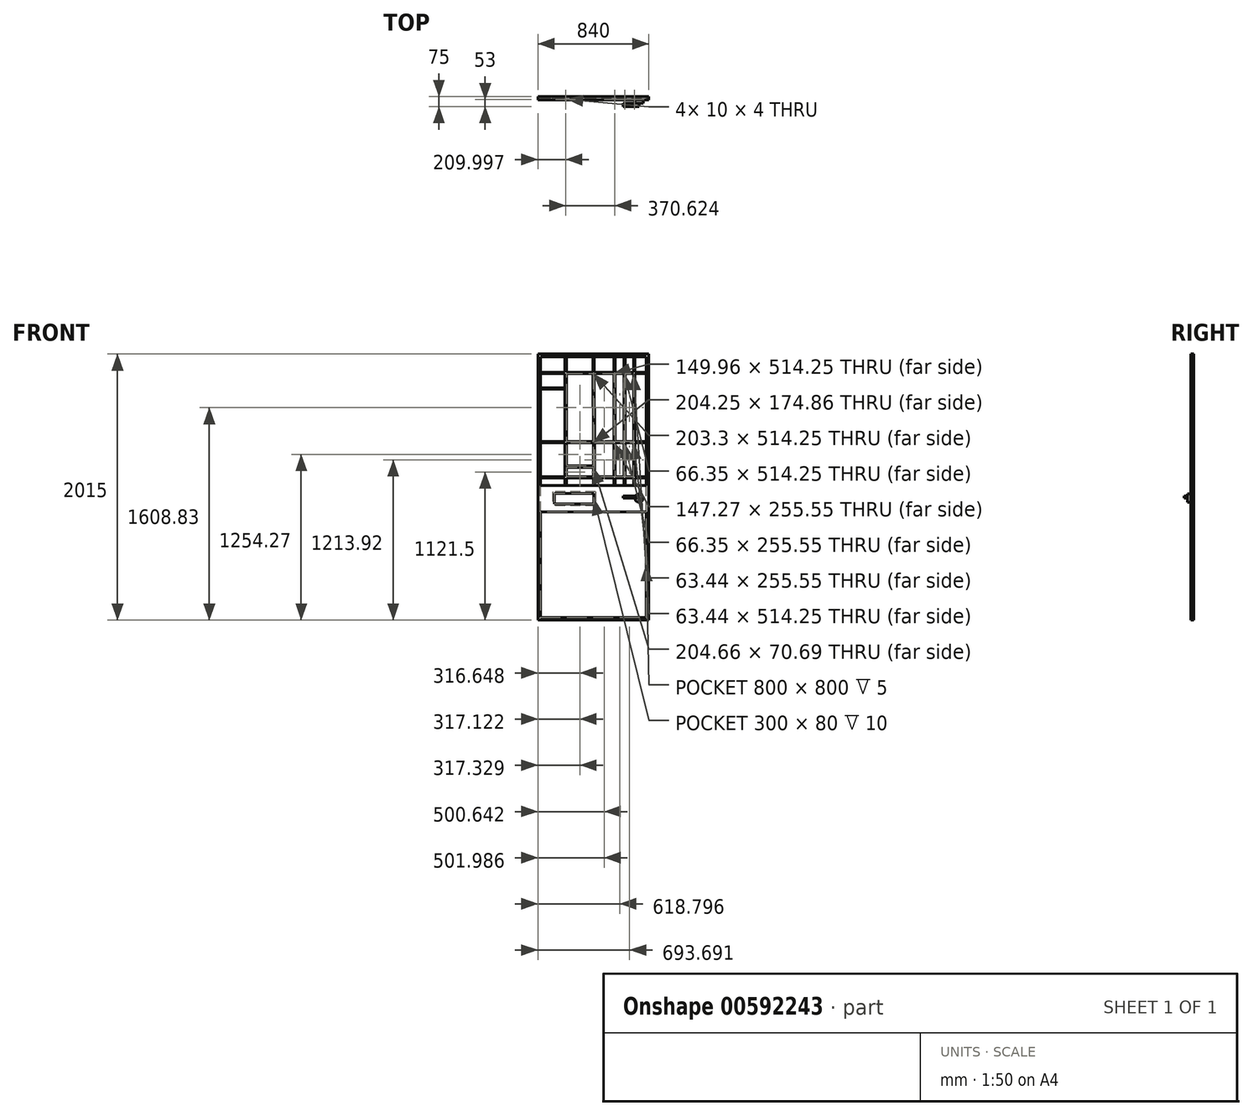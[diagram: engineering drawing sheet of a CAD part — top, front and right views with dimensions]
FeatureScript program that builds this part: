
annotation { "Feature Type Name" : "Feature", "Feature Type Description" : "" }
export const myFeature = defineFeature(function(context is Context, id is Id, definition is map)
    precondition{}
    {
        {
            var Q0;
            Q0=qCreatedBy(makeId("Front.planeOp"),FACE);
            var sketch = newSketch(context, id + "F0", { "sketchPlane" : qUnion([Q0])});
            skLineSegment(sketch, "E0.bottom", {"start": v(0, 0) * mm, "end": v(840, 0) * mm});
            skLineSegment(sketch, "E0.top", {"start": v(0, 2015) * mm, "end": v(840, 2015) * mm});
            skLineSegment(sketch, "E0.left", {"start": v(0, 0) * mm, "end": v(0, 2015) * mm});
            skLineSegment(sketch, "E0.right", {"start": v(840, 0) * mm, "end": v(840, 2015) * mm});
            skLineSegment(sketch, "E1.0", {"start": v(20, 1995) * mm, "end": v(820, 1995) * mm});
            skLineSegment(sketch, "E1.1", {"start": v(20, 20) * mm, "end": v(20, 1995) * mm});
            skLineSegment(sketch, "E1.2", {"start": v(20, 20) * mm, "end": v(820, 20) * mm});
            skLineSegment(sketch, "E1.3", {"start": v(820, 20) * mm, "end": v(820, 1995) * mm});
            skLineSegment(sketch, "E2.bottom", {"start": v(20, 1020) * mm, "end": v(820, 1020) * mm});
            skLineSegment(sketch, "E2.top", {"start": v(20, 820) * mm, "end": v(820, 820) * mm});
            skLineSegment(sketch, "E2.left", {"start": v(20, 1020) * mm, "end": v(20, 820) * mm});
            skLineSegment(sketch, "E2.right", {"start": v(820, 1020) * mm, "end": v(820, 820) * mm});
            skLineSegment(sketch, "E3.bottom", {"start": v(205, 1995) * mm, "end": v(215, 1995) * mm});
            skLineSegment(sketch, "E3.top", {"start": v(205, 1020) * mm, "end": v(215, 1020) * mm});
            skLineSegment(sketch, "E3.left", {"start": v(205, 1995) * mm, "end": v(205, 1875.95) * mm});
            skLineSegment(sketch, "E3.right", {"start": v(215, 1995) * mm, "end": v(215, 1875.95) * mm});
            skLineSegment(sketch, "E4.bottom", {"start": v(735.41, 1995) * mm, "end": v(725.41, 1995) * mm});
            skLineSegment(sketch, "E4.top", {"start": v(735.41, 1020) * mm, "end": v(725.41, 1020) * mm});
            skLineSegment(sketch, "E4.left", {"start": v(735.41, 1995) * mm, "end": v(735.41, 1875.95) * mm});
            skLineSegment(sketch, "E4.right", {"start": v(725.41, 1995) * mm, "end": v(725.41, 1875.95) * mm});
            skLineSegment(sketch, "E5", {"start": v(420, 1995) * mm, "end": v(420, 1930.7) * mm, "construction": true});
            skLineSegment(sketch, "E6.bottom", {"start": v(415, 1995) * mm, "end": v(425, 1995) * mm});
            skLineSegment(sketch, "E6.top", {"start": v(420, 1020) * mm, "end": v(430, 1020) * mm});
            skLineSegment(sketch, "E6.left", {"start": v(415, 1995) * mm, "end": v(415.61, 1875.95) * mm});
            skLineSegment(sketch, "E6.right", {"start": v(425, 1995) * mm, "end": v(428.3, 1351.7) * mm});
            skLineSegment(sketch, "E7.bottom", {"start": v(575.62, 1995) * mm, "end": v(585.62, 1995) * mm});
            skLineSegment(sketch, "E7.top", {"start": v(575.62, 1020) * mm, "end": v(585.62, 1020) * mm});
            skLineSegment(sketch, "E7.left", {"start": v(575.62, 1995) * mm, "end": v(575.62, 1875.95) * mm});
            skLineSegment(sketch, "E7.right", {"start": v(585.62, 1995) * mm, "end": v(585.62, 1875.95) * mm});
            skLineSegment(sketch, "E8.bottom", {"start": v(651.97, 1995) * mm, "end": v(661.97, 1995) * mm});
            skLineSegment(sketch, "E8.top", {"start": v(651.97, 1020) * mm, "end": v(661.97, 1020) * mm});
            skLineSegment(sketch, "E8.left", {"start": v(651.97, 1995) * mm, "end": v(651.97, 1875.95) * mm});
            skLineSegment(sketch, "E8.right", {"start": v(661.97, 1995) * mm, "end": v(661.97, 1875.95) * mm});
            skLineSegment(sketch, "E9.bottom", {"start": v(20, 1875.95) * mm, "end": v(205, 1875.95) * mm});
            skLineSegment(sketch, "E9.top", {"start": v(20, 1865.95) * mm, "end": v(205, 1865.95) * mm});
            skLineSegment(sketch, "E9.left", {"start": v(20, 1875.95) * mm, "end": v(20, 1865.95) * mm});
            skLineSegment(sketch, "E9.right", {"start": v(820, 1875.95) * mm, "end": v(820, 1865.95) * mm});
            skLineSegment(sketch, "E10.bottom", {"start": v(20, 1086.15) * mm, "end": v(205, 1086.15) * mm});
            skLineSegment(sketch, "E10.top", {"start": v(20, 1076.15) * mm, "end": v(205, 1076.15) * mm});
            skLineSegment(sketch, "E10.left", {"start": v(20, 1086.15) * mm, "end": v(20, 1076.15) * mm});
            skLineSegment(sketch, "E10.right", {"start": v(820, 1086.15) * mm, "end": v(820, 1076.15) * mm});
            skLineSegment(sketch, "E11.bottom", {"start": v(215, 1166.84) * mm, "end": v(419.3, 1166.84) * mm});
            skLineSegment(sketch, "E11.top", {"start": v(215, 1156.84) * mm, "end": v(419.3, 1156.84) * mm});
            skLineSegment(sketch, "E12.bottom", {"start": v(20, 1351.7) * mm, "end": v(205, 1351.7) * mm});
            skLineSegment(sketch, "E12.top", {"start": v(20, 1341.7) * mm, "end": v(205, 1341.7) * mm});
            skLineSegment(sketch, "E12.left", {"start": v(20, 1351.7) * mm, "end": v(20, 1341.7) * mm});
            skLineSegment(sketch, "E12.right", {"start": v(820, 1351.7) * mm, "end": v(820, 1341.7) * mm});
            skLineSegment(sketch, "E13.bottom", {"start": v(20, 1757.88) * mm, "end": v(205, 1757.88) * mm});
            skLineSegment(sketch, "E13.top", {"start": v(20, 1747.88) * mm, "end": v(205, 1747.88) * mm});
            skLineSegment(sketch, "E13.left", {"start": v(20, 1757.88) * mm, "end": v(20, 1747.88) * mm});
            skLineSegment(sketch, "E14.trimOffspring", {"start": v(215, 1076.15) * mm, "end": v(419.71, 1076.15) * mm});
            skLineSegment(sketch, "E15.trimOffspring", {"start": v(215, 1086.15) * mm, "end": v(419.66, 1086.15) * mm});
            skLineSegment(sketch, "E16.trimOffspring", {"start": v(215, 1076.15) * mm, "end": v(215, 1020) * mm});
            skLineSegment(sketch, "E17.trimOffspring", {"start": v(205, 1076.15) * mm, "end": v(205, 1020) * mm});
            skLineSegment(sketch, "E18.trimOffspring", {"start": v(419.3, 1156.84) * mm, "end": v(419.66, 1086.15) * mm});
            skLineSegment(sketch, "E19.trimOffspring", {"start": v(419.71, 1076.15) * mm, "end": v(420, 1020) * mm});
            skLineSegment(sketch, "E20.trimOffspring", {"start": v(429.66, 1086.15) * mm, "end": v(575.62, 1086.15) * mm});
            skLineSegment(sketch, "E21.trimOffspring", {"start": v(429.71, 1076.15) * mm, "end": v(430, 1020) * mm});
            skLineSegment(sketch, "E22.trimOffspring", {"start": v(429.71, 1076.15) * mm, "end": v(575.62, 1076.15) * mm});
            skLineSegment(sketch, "E23.trimOffspring", {"start": v(575.62, 1076.15) * mm, "end": v(575.62, 1020) * mm});
            skLineSegment(sketch, "E24.trimOffspring", {"start": v(585.62, 1076.15) * mm, "end": v(585.62, 1020) * mm});
            skLineSegment(sketch, "E25.trimOffspring", {"start": v(585.62, 1086.15) * mm, "end": v(651.97, 1086.15) * mm});
            skLineSegment(sketch, "E26.trimOffspring", {"start": v(585.62, 1076.15) * mm, "end": v(651.97, 1076.15) * mm});
            skLineSegment(sketch, "E27.trimOffspring", {"start": v(651.97, 1076.15) * mm, "end": v(651.97, 1020) * mm});
            skLineSegment(sketch, "E28.trimOffspring", {"start": v(661.97, 1076.15) * mm, "end": v(661.97, 1020) * mm});
            skLineSegment(sketch, "E29.trimOffspring", {"start": v(661.97, 1086.15) * mm, "end": v(725.41, 1086.15) * mm});
            skLineSegment(sketch, "E30.trimOffspring", {"start": v(661.97, 1076.15) * mm, "end": v(725.41, 1076.15) * mm});
            skLineSegment(sketch, "E31.trimOffspring", {"start": v(215, 1156.84) * mm, "end": v(215, 1086.15) * mm});
            skLineSegment(sketch, "E32.trimOffspring", {"start": v(205, 1341.7) * mm, "end": v(205, 1086.15) * mm});
            skLineSegment(sketch, "E33.trimOffspring", {"start": v(215, 1351.7) * mm, "end": v(418.3, 1351.7) * mm});
            skLineSegment(sketch, "E34.trimOffspring", {"start": v(215, 1341.7) * mm, "end": v(418.35, 1341.7) * mm});
            skLineSegment(sketch, "E35.trimOffspring", {"start": v(215, 1341.7) * mm, "end": v(215, 1166.84) * mm});
            skLineSegment(sketch, "E36.trimOffspring", {"start": v(428.35, 1341.7) * mm, "end": v(429.66, 1086.15) * mm});
            skLineSegment(sketch, "E37.trimOffspring", {"start": v(418.35, 1341.7) * mm, "end": v(419.25, 1166.84) * mm});
            skLineSegment(sketch, "E38.trimOffspring", {"start": v(428.35, 1341.7) * mm, "end": v(575.62, 1341.7) * mm});
            skLineSegment(sketch, "E39.trimOffspring", {"start": v(428.3, 1351.7) * mm, "end": v(575.62, 1351.7) * mm});
            skLineSegment(sketch, "E40.trimOffspring", {"start": v(215, 1865.95) * mm, "end": v(215, 1351.7) * mm});
            skLineSegment(sketch, "E41.trimOffspring", {"start": v(215, 1875.95) * mm, "end": v(415.61, 1875.95) * mm});
            skLineSegment(sketch, "E42.trimOffspring", {"start": v(205, 1865.95) * mm, "end": v(205, 1757.88) * mm});
            skLineSegment(sketch, "E43.trimOffspring", {"start": v(215, 1865.95) * mm, "end": v(415.66, 1865.95) * mm});
            skLineSegment(sketch, "E44.trimOffspring", {"start": v(205, 1747.88) * mm, "end": v(205, 1351.7) * mm});
            skLineSegment(sketch, "E45.trimOffspring", {"start": v(425.61, 1875.95) * mm, "end": v(575.62, 1875.95) * mm});
            skLineSegment(sketch, "E46.trimOffspring", {"start": v(415.66, 1865.95) * mm, "end": v(418.3, 1351.7) * mm});
            skLineSegment(sketch, "E47.trimOffspring", {"start": v(425.66, 1865.95) * mm, "end": v(575.62, 1865.95) * mm});
            skLineSegment(sketch, "E48.trimOffspring", {"start": v(575.62, 1865.95) * mm, "end": v(575.62, 1351.7) * mm});
            skLineSegment(sketch, "E49.trimOffspring", {"start": v(585.62, 1875.95) * mm, "end": v(651.97, 1875.95) * mm});
            skLineSegment(sketch, "E50.trimOffspring", {"start": v(585.62, 1865.95) * mm, "end": v(585.62, 1351.7) * mm});
            skLineSegment(sketch, "E51.trimOffspring", {"start": v(585.62, 1865.95) * mm, "end": v(651.97, 1865.95) * mm});
            skLineSegment(sketch, "E52.trimOffspring", {"start": v(651.97, 1865.95) * mm, "end": v(651.97, 1351.7) * mm});
            skLineSegment(sketch, "E53.trimOffspring", {"start": v(661.97, 1875.95) * mm, "end": v(725.41, 1875.95) * mm});
            skLineSegment(sketch, "E54.trimOffspring", {"start": v(661.97, 1865.95) * mm, "end": v(725.41, 1865.95) * mm});
            skLineSegment(sketch, "E55.trimOffspring", {"start": v(661.97, 1865.95) * mm, "end": v(661.97, 1351.7) * mm});
            skLineSegment(sketch, "E56.trimOffspring", {"start": v(725.41, 1865.95) * mm, "end": v(725.41, 1351.7) * mm});
            skLineSegment(sketch, "E57.trimOffspring", {"start": v(735.41, 1875.95) * mm, "end": v(820, 1875.95) * mm});
            skLineSegment(sketch, "E58.trimOffspring", {"start": v(735.41, 1865.95) * mm, "end": v(735.41, 1351.7) * mm});
            skLineSegment(sketch, "E59.trimOffspring", {"start": v(735.41, 1865.95) * mm, "end": v(820, 1865.95) * mm});
            skLineSegment(sketch, "E60.trimOffspring", {"start": v(585.62, 1351.7) * mm, "end": v(651.97, 1351.7) * mm});
            skLineSegment(sketch, "E61.trimOffspring", {"start": v(585.62, 1341.7) * mm, "end": v(651.97, 1341.7) * mm});
            skLineSegment(sketch, "E62.trimOffspring", {"start": v(575.62, 1341.7) * mm, "end": v(575.62, 1086.15) * mm});
            skLineSegment(sketch, "E63.trimOffspring", {"start": v(585.62, 1341.7) * mm, "end": v(585.62, 1086.15) * mm});
            skLineSegment(sketch, "E64.trimOffspring", {"start": v(651.97, 1341.7) * mm, "end": v(651.97, 1086.15) * mm});
            skLineSegment(sketch, "E65.trimOffspring", {"start": v(661.97, 1351.7) * mm, "end": v(725.41, 1351.7) * mm});
            skLineSegment(sketch, "E66.trimOffspring", {"start": v(661.97, 1341.7) * mm, "end": v(725.41, 1341.7) * mm});
            skLineSegment(sketch, "E67.trimOffspring", {"start": v(661.97, 1341.7) * mm, "end": v(661.97, 1086.15) * mm});
            skLineSegment(sketch, "E68.trimOffspring", {"start": v(725.41, 1341.7) * mm, "end": v(725.41, 1086.15) * mm});
            skLineSegment(sketch, "E69.trimOffspring", {"start": v(735.41, 1351.7) * mm, "end": v(820, 1351.7) * mm});
            skLineSegment(sketch, "E70.trimOffspring", {"start": v(735.41, 1341.7) * mm, "end": v(735.41, 1086.15) * mm});
            skLineSegment(sketch, "E71.trimOffspring", {"start": v(735.41, 1341.7) * mm, "end": v(820, 1341.7) * mm});
            skLineSegment(sketch, "E72.trimOffspring", {"start": v(735.41, 1076.15) * mm, "end": v(820, 1076.15) * mm});
            skLineSegment(sketch, "E73.trimOffspring", {"start": v(735.41, 1086.15) * mm, "end": v(820, 1086.15) * mm});
            skLineSegment(sketch, "E74.trimOffspring", {"start": v(735.41, 1076.15) * mm, "end": v(735.41, 1020) * mm});
            skLineSegment(sketch, "E75.trimOffspring", {"start": v(725.41, 1076.15) * mm, "end": v(725.41, 1020) * mm});
            skSolve(sketch);
        }
        {
            var Q0;
            Q0 = qSketchRegion(id + "F0", true);
            extrude(context, id + "F1", {"entities" : qUnion([Q0]), "oppositeDirection" : true, "depth" : 20 * mm, "offsetDistance" : 25 * mm, "hasSecondDirection" : true, "secondDirectionOppositeDirection" : false, "secondDirectionDepth" : 5 * mm});
        }
        {
            var Q0;
            {var subQ0=sQuery(id+"F0.wireOp",EDGE,"E1.2");Q0=makeQuery(id+"F0.imprint","IMPRINT",FACE,{"disambiguationData":[TD([[makeQuery(id+"F0.imprint","IMPRINT",EDGE,{"derivedFrom":subQ0}),1.0]])]});}
            extrude(context, id + "F2", {"entities" : qUnion([Q0]), "operationType" : NewBodyOperationType.ADD, "oppositeDirection" : true, "depth" : 5 * mm, "offsetDistance" : 25 * mm});
        }
        {
            var Q0;
            Q0=makeQuery(id+"F0.imprint","IMPRINT",FACE,{"disambiguationData":[TD([[makeQuery(id+"F0.imprint","IMPRINT",EDGE,{"derivedFrom":sQuery(id+"F0.wireOp",EDGE,"E2.top")}),1.0]])]});
            extrude(context, id + "F3", {"entities" : qUnion([Q0]), "operationType" : NewBodyOperationType.ADD, "depth" : 5 * mm, "offsetDistance" : 25 * mm, "hasSecondDirection" : true, "secondDirectionOppositeDirection" : true, "secondDirectionDepth" : 5 * mm});
        }
        {
            var Q0;
            Q0=makeQuery(id+"F0.imprint","IMPRINT",FACE,{"disambiguationData":[TD([[makeQuery(id+"F0.imprint","IMPRINT",EDGE,{"derivedFrom":sQuery(id+"F0.wireOp",EDGE,"E3.bottom")}),-1.0]])]});
            var Q1;
            Q1=makeQuery(id+"F0.imprint","IMPRINT",FACE,{"disambiguationData":[TD([[makeQuery(id+"F0.imprint","IMPRINT",EDGE,{"derivedFrom":sQuery(id+"F0.wireOp",EDGE,"E6.bottom")}),-1.0]])]});
            var Q2;
            Q2=makeQuery(id+"F0.imprint","IMPRINT",FACE,{"disambiguationData":[TD([[makeQuery(id+"F0.imprint","IMPRINT",EDGE,{"derivedFrom":sQuery(id+"F0.wireOp",EDGE,"E4.bottom")}),1.0]])]});
            var Q3;
            {var subQ5=sQuery(id+"F0.wireOp",EDGE,"E9.left");Q3=makeQuery(id+"F0.imprint","IMPRINT",FACE,{"disambiguationData":[TD([[makeQuery(id+"F0.imprint","IMPRINT",EDGE,{"derivedFrom":subQ5}),1.0]])]});}
            var Q4;
            {var subQ0=sQuery(id+"F0.wireOp",EDGE,"E9.bottom");var subQ1=sQuery(id+"F0.wireOp",EDGE,"E3.left");var subQ2=makeQuery(id+"F0.imprint","INTERSECT",VERTEX,{"derivedFrom":[subQ1,subQ0]});Q4=makeQuery(id+"F0.imprint","IMPRINT",FACE,{"disambiguationData":[TD([[makeQuery(id+"F0.imprint","IMPRINT",EDGE,{"disambiguationData":[TD([[subQ2,-1.0]])],"derivedFrom":subQ1}),1.0]])]});}
            var Q5;
            {var subQ0=sQuery(id+"F0.wireOp",EDGE,"E9.bottom");var subQ1=sQuery(id+"F0.wireOp",EDGE,"E6.left");var subQ2=makeQuery(id+"F0.imprint","INTERSECT",VERTEX,{"derivedFrom":[subQ1,subQ0]});Q5=makeQuery(id+"F0.imprint","IMPRINT",FACE,{"disambiguationData":[TD([[makeQuery(id+"F0.imprint","IMPRINT",EDGE,{"disambiguationData":[TD([[subQ2,-1.0]])],"derivedFrom":subQ1}),1.0]])]});}
            var Q6;
            {var subQ0=sQuery(id+"F0.wireOp",EDGE,"E9.top");var subQ1=sQuery(id+"F0.wireOp",EDGE,"E6.left");var subQ2=makeQuery(id+"F0.imprint","INTERSECT",VERTEX,{"derivedFrom":[subQ1,subQ0]});Q6=makeQuery(id+"F0.imprint","IMPRINT",FACE,{"disambiguationData":[TD([[makeQuery(id+"F0.imprint","IMPRINT",EDGE,{"disambiguationData":[TD([[subQ2,-1.0]])],"derivedFrom":subQ1}),1.0]])]});}
            var Q7;
            {var subQ7=sQuery(id+"F0.wireOp",EDGE,"E13.right");Q7=makeQuery(id+"F0.imprint","IMPRINT",FACE,{"disambiguationData":[TD([[makeQuery(id+"F0.imprint","IMPRINT",EDGE,{"derivedFrom":subQ7}),1.0]])]});}
            var Q8;
            Q8=makeQuery(id+"F0.imprint","IMPRINT",FACE,{"disambiguationData":[TD([[makeQuery(id+"F0.imprint","IMPRINT",EDGE,{"derivedFrom":sQuery(id+"F0.wireOp",EDGE,"E13.bottom")}),-1.0]])]});
            var Q9;
            {var subQ0=sQuery(id+"F0.wireOp",EDGE,"E7.bottom");Q9=makeQuery(id+"F0.imprint","IMPRINT",FACE,{"disambiguationData":[TD([[makeQuery(id+"F0.imprint","IMPRINT",EDGE,{"derivedFrom":subQ0}),-1.0]])]});}
            var Q10;
            {var subQ0=sQuery(id+"F0.wireOp",EDGE,"E8.bottom");Q10=makeQuery(id+"F0.imprint","IMPRINT",FACE,{"disambiguationData":[TD([[makeQuery(id+"F0.imprint","IMPRINT",EDGE,{"derivedFrom":subQ0}),-1.0]])]});}
            var Q11;
            {var subQ0=sQuery(id+"F0.wireOp",EDGE,"E9.top");var subQ1=sQuery(id+"F0.wireOp",EDGE,"E8.left");var subQ2=makeQuery(id+"F0.imprint","INTERSECT",VERTEX,{"derivedFrom":[subQ1,subQ0]});Q11=makeQuery(id+"F0.imprint","IMPRINT",FACE,{"disambiguationData":[TD([[makeQuery(id+"F0.imprint","IMPRINT",EDGE,{"disambiguationData":[TD([[subQ2,-1.0]])],"derivedFrom":subQ1}),1.0]])]});}
            var Q12;
            {var subQ0=sQuery(id+"F0.wireOp",EDGE,"E9.bottom");var subQ1=sQuery(id+"F0.wireOp",EDGE,"E8.left");var subQ2=makeQuery(id+"F0.imprint","INTERSECT",VERTEX,{"derivedFrom":[subQ1,subQ0]});Q12=makeQuery(id+"F0.imprint","IMPRINT",FACE,{"disambiguationData":[TD([[makeQuery(id+"F0.imprint","IMPRINT",EDGE,{"disambiguationData":[TD([[subQ2,-1.0]])],"derivedFrom":subQ1}),1.0]])]});}
            var Q13;
            {var subQ0=sQuery(id+"F0.wireOp",EDGE,"E9.top");var subQ1=sQuery(id+"F0.wireOp",EDGE,"E7.left");var subQ2=makeQuery(id+"F0.imprint","INTERSECT",VERTEX,{"derivedFrom":[subQ1,subQ0]});Q13=makeQuery(id+"F0.imprint","IMPRINT",FACE,{"disambiguationData":[TD([[makeQuery(id+"F0.imprint","IMPRINT",EDGE,{"disambiguationData":[TD([[subQ2,-1.0]])],"derivedFrom":subQ1}),1.0]])]});}
            var Q14;
            {var subQ5=sQuery(id+"F0.wireOp",EDGE,"E9.right");Q14=makeQuery(id+"F0.imprint","IMPRINT",FACE,{"disambiguationData":[TD([[makeQuery(id+"F0.imprint","IMPRINT",EDGE,{"derivedFrom":subQ5}),-1.0]])]});}
            var Q15;
            {var subQ0=sQuery(id+"F0.wireOp",EDGE,"E9.top");var subQ1=sQuery(id+"F0.wireOp",EDGE,"E4.left");var subQ2=makeQuery(id+"F0.imprint","INTERSECT",VERTEX,{"derivedFrom":[subQ1,subQ0]});Q15=makeQuery(id+"F0.imprint","IMPRINT",FACE,{"disambiguationData":[TD([[makeQuery(id+"F0.imprint","IMPRINT",EDGE,{"disambiguationData":[TD([[subQ2,-1.0]])],"derivedFrom":subQ1}),-1.0]])]});}
            var Q16;
            {var subQ0=sQuery(id+"F0.wireOp",EDGE,"E9.bottom");var subQ1=sQuery(id+"F0.wireOp",EDGE,"E4.left");var subQ2=makeQuery(id+"F0.imprint","INTERSECT",VERTEX,{"derivedFrom":[subQ1,subQ0]});Q16=makeQuery(id+"F0.imprint","IMPRINT",FACE,{"disambiguationData":[TD([[makeQuery(id+"F0.imprint","IMPRINT",EDGE,{"disambiguationData":[TD([[subQ2,-1.0]])],"derivedFrom":subQ1}),-1.0]])]});}
            var Q17;
            {var subQ0=sQuery(id+"F0.wireOp",EDGE,"E9.bottom");var subQ1=sQuery(id+"F0.wireOp",EDGE,"E7.left");var subQ2=makeQuery(id+"F0.imprint","INTERSECT",VERTEX,{"derivedFrom":[subQ1,subQ0]});Q17=makeQuery(id+"F0.imprint","IMPRINT",FACE,{"disambiguationData":[TD([[makeQuery(id+"F0.imprint","IMPRINT",EDGE,{"disambiguationData":[TD([[subQ2,-1.0]])],"derivedFrom":subQ1}),1.0]])]});}
            var Q18;
            {var subQ5=sQuery(id+"F0.wireOp",EDGE,"E12.left");Q18=makeQuery(id+"F0.imprint","IMPRINT",FACE,{"disambiguationData":[TD([[makeQuery(id+"F0.imprint","IMPRINT",EDGE,{"derivedFrom":subQ5}),1.0]])]});}
            var Q19;
            {var subQ0=sQuery(id+"F0.wireOp",EDGE,"E11.left");Q19=makeQuery(id+"F0.imprint","IMPRINT",FACE,{"disambiguationData":[TD([[makeQuery(id+"F0.imprint","IMPRINT",EDGE,{"derivedFrom":subQ0}),-1.0]])]});}
            var Q20;
            {var subQ0=sQuery(id+"F0.wireOp",EDGE,"E12.bottom");var subQ1=sQuery(id+"F0.wireOp",EDGE,"E3.left");var subQ2=makeQuery(id+"F0.imprint","INTERSECT",VERTEX,{"derivedFrom":[subQ1,subQ0]});Q20=makeQuery(id+"F0.imprint","IMPRINT",FACE,{"disambiguationData":[TD([[makeQuery(id+"F0.imprint","IMPRINT",EDGE,{"disambiguationData":[TD([[subQ2,-1.0]])],"derivedFrom":subQ1}),1.0]])]});}
            var Q21;
            {var subQ5=sQuery(id+"F0.wireOp",EDGE,"E11.right");Q21=makeQuery(id+"F0.imprint","IMPRINT",FACE,{"disambiguationData":[TD([[makeQuery(id+"F0.imprint","IMPRINT",EDGE,{"derivedFrom":subQ5}),1.0]])]});}
            var Q22;
            {var subQ0=sQuery(id+"F0.wireOp",EDGE,"E12.bottom");var subQ1=sQuery(id+"F0.wireOp",EDGE,"E6.left");var subQ2=makeQuery(id+"F0.imprint","INTERSECT",VERTEX,{"derivedFrom":[subQ1,subQ0]});Q22=makeQuery(id+"F0.imprint","IMPRINT",FACE,{"disambiguationData":[TD([[makeQuery(id+"F0.imprint","IMPRINT",EDGE,{"disambiguationData":[TD([[subQ2,-1.0]])],"derivedFrom":subQ1}),1.0]])]});}
            var Q23;
            {var subQ0=sQuery(id+"F0.wireOp",EDGE,"E12.bottom");var subQ1=sQuery(id+"F0.wireOp",EDGE,"E7.left");var subQ2=makeQuery(id+"F0.imprint","INTERSECT",VERTEX,{"derivedFrom":[subQ1,subQ0]});Q23=makeQuery(id+"F0.imprint","IMPRINT",FACE,{"disambiguationData":[TD([[makeQuery(id+"F0.imprint","IMPRINT",EDGE,{"disambiguationData":[TD([[subQ2,-1.0]])],"derivedFrom":subQ1}),1.0]])]});}
            var Q24;
            {var subQ0=sQuery(id+"F0.wireOp",EDGE,"E12.bottom");var subQ1=sQuery(id+"F0.wireOp",EDGE,"E8.left");var subQ2=makeQuery(id+"F0.imprint","INTERSECT",VERTEX,{"derivedFrom":[subQ1,subQ0]});Q24=makeQuery(id+"F0.imprint","IMPRINT",FACE,{"disambiguationData":[TD([[makeQuery(id+"F0.imprint","IMPRINT",EDGE,{"disambiguationData":[TD([[subQ2,-1.0]])],"derivedFrom":subQ1}),1.0]])]});}
            var Q25;
            {var subQ0=sQuery(id+"F0.wireOp",EDGE,"E12.bottom");var subQ1=sQuery(id+"F0.wireOp",EDGE,"E4.left");var subQ2=makeQuery(id+"F0.imprint","INTERSECT",VERTEX,{"derivedFrom":[subQ1,subQ0]});Q25=makeQuery(id+"F0.imprint","IMPRINT",FACE,{"disambiguationData":[TD([[makeQuery(id+"F0.imprint","IMPRINT",EDGE,{"disambiguationData":[TD([[subQ2,-1.0]])],"derivedFrom":subQ1}),-1.0]])]});}
            var Q26;
            {var subQ5=sQuery(id+"F0.wireOp",EDGE,"E12.right");Q26=makeQuery(id+"F0.imprint","IMPRINT",FACE,{"disambiguationData":[TD([[makeQuery(id+"F0.imprint","IMPRINT",EDGE,{"derivedFrom":subQ5}),-1.0]])]});}
            var Q27;
            {var subQ0=sQuery(id+"F0.wireOp",EDGE,"E12.top");var subQ1=sQuery(id+"F0.wireOp",EDGE,"E4.left");var subQ2=makeQuery(id+"F0.imprint","INTERSECT",VERTEX,{"derivedFrom":[subQ1,subQ0]});Q27=makeQuery(id+"F0.imprint","IMPRINT",FACE,{"disambiguationData":[TD([[makeQuery(id+"F0.imprint","IMPRINT",EDGE,{"disambiguationData":[TD([[subQ2,-1.0]])],"derivedFrom":subQ1}),-1.0]])]});}
            var Q28;
            {var subQ0=sQuery(id+"F0.wireOp",EDGE,"E12.top");var subQ1=sQuery(id+"F0.wireOp",EDGE,"E8.left");var subQ2=makeQuery(id+"F0.imprint","INTERSECT",VERTEX,{"derivedFrom":[subQ1,subQ0]});Q28=makeQuery(id+"F0.imprint","IMPRINT",FACE,{"disambiguationData":[TD([[makeQuery(id+"F0.imprint","IMPRINT",EDGE,{"disambiguationData":[TD([[subQ2,-1.0]])],"derivedFrom":subQ1}),1.0]])]});}
            var Q29;
            {var subQ0=sQuery(id+"F0.wireOp",EDGE,"E12.top");var subQ1=sQuery(id+"F0.wireOp",EDGE,"E7.left");var subQ2=makeQuery(id+"F0.imprint","INTERSECT",VERTEX,{"derivedFrom":[subQ1,subQ0]});Q29=makeQuery(id+"F0.imprint","IMPRINT",FACE,{"disambiguationData":[TD([[makeQuery(id+"F0.imprint","IMPRINT",EDGE,{"disambiguationData":[TD([[subQ2,-1.0]])],"derivedFrom":subQ1}),1.0]])]});}
            var Q30;
            {var subQ0=sQuery(id+"F0.wireOp",EDGE,"E4.top");Q30=makeQuery(id+"F0.imprint","IMPRINT",FACE,{"disambiguationData":[TD([[makeQuery(id+"F0.imprint","IMPRINT",EDGE,{"derivedFrom":subQ0}),-1.0]])]});}
            var Q31;
            {var subQ5=sQuery(id+"F0.wireOp",EDGE,"E10.right");Q31=makeQuery(id+"F0.imprint","IMPRINT",FACE,{"disambiguationData":[TD([[makeQuery(id+"F0.imprint","IMPRINT",EDGE,{"derivedFrom":subQ5}),-1.0]])]});}
            var Q32;
            {var subQ0=sQuery(id+"F0.wireOp",EDGE,"E10.bottom");var subQ1=sQuery(id+"F0.wireOp",EDGE,"E4.left");var subQ2=makeQuery(id+"F0.imprint","INTERSECT",VERTEX,{"derivedFrom":[subQ1,subQ0]});Q32=makeQuery(id+"F0.imprint","IMPRINT",FACE,{"disambiguationData":[TD([[makeQuery(id+"F0.imprint","IMPRINT",EDGE,{"disambiguationData":[TD([[subQ2,-1.0]])],"derivedFrom":subQ1}),-1.0]])]});}
            var Q33;
            {var subQ0=sQuery(id+"F0.wireOp",EDGE,"E10.bottom");var subQ1=sQuery(id+"F0.wireOp",EDGE,"E8.left");var subQ2=makeQuery(id+"F0.imprint","INTERSECT",VERTEX,{"derivedFrom":[subQ1,subQ0]});Q33=makeQuery(id+"F0.imprint","IMPRINT",FACE,{"disambiguationData":[TD([[makeQuery(id+"F0.imprint","IMPRINT",EDGE,{"disambiguationData":[TD([[subQ2,-1.0]])],"derivedFrom":subQ1}),1.0]])]});}
            var Q34;
            {var subQ0=sQuery(id+"F0.wireOp",EDGE,"E8.top");Q34=makeQuery(id+"F0.imprint","IMPRINT",FACE,{"disambiguationData":[TD([[makeQuery(id+"F0.imprint","IMPRINT",EDGE,{"derivedFrom":subQ0}),1.0]])]});}
            var Q35;
            {var subQ0=sQuery(id+"F0.wireOp",EDGE,"E10.bottom");var subQ1=sQuery(id+"F0.wireOp",EDGE,"E7.left");var subQ2=makeQuery(id+"F0.imprint","INTERSECT",VERTEX,{"derivedFrom":[subQ1,subQ0]});Q35=makeQuery(id+"F0.imprint","IMPRINT",FACE,{"disambiguationData":[TD([[makeQuery(id+"F0.imprint","IMPRINT",EDGE,{"disambiguationData":[TD([[subQ2,-1.0]])],"derivedFrom":subQ1}),1.0]])]});}
            var Q36;
            {var subQ0=sQuery(id+"F0.wireOp",EDGE,"E7.top");Q36=makeQuery(id+"F0.imprint","IMPRINT",FACE,{"disambiguationData":[TD([[makeQuery(id+"F0.imprint","IMPRINT",EDGE,{"derivedFrom":subQ0}),1.0]])]});}
            var Q37;
            {var subQ0=sQuery(id+"F0.wireOp",EDGE,"E6.top");Q37=makeQuery(id+"F0.imprint","IMPRINT",FACE,{"disambiguationData":[TD([[makeQuery(id+"F0.imprint","IMPRINT",EDGE,{"derivedFrom":subQ0}),1.0]])]});}
            var Q38;
            {var subQ5=sQuery(id+"F0.wireOp",EDGE,"E10.left");Q38=makeQuery(id+"F0.imprint","IMPRINT",FACE,{"disambiguationData":[TD([[makeQuery(id+"F0.imprint","IMPRINT",EDGE,{"derivedFrom":subQ5}),1.0]])]});}
            var Q39;
            {var subQ0=sQuery(id+"F0.wireOp",EDGE,"E3.top");Q39=makeQuery(id+"F0.imprint","IMPRINT",FACE,{"disambiguationData":[TD([[makeQuery(id+"F0.imprint","IMPRINT",EDGE,{"derivedFrom":subQ0}),1.0]])]});}
            var Q40;
            {var subQ0=sQuery(id+"F0.wireOp",EDGE,"E10.bottom");var subQ1=sQuery(id+"F0.wireOp",EDGE,"E6.left");var subQ2=makeQuery(id+"F0.imprint","INTERSECT",VERTEX,{"derivedFrom":[subQ1,subQ0]});Q40=makeQuery(id+"F0.imprint","IMPRINT",FACE,{"disambiguationData":[TD([[makeQuery(id+"F0.imprint","IMPRINT",EDGE,{"disambiguationData":[TD([[subQ2,-1.0]])],"derivedFrom":subQ1}),1.0]])]});}
            var Q41;
            {var subQ0=sQuery(id+"F0.wireOp",EDGE,"E10.bottom");var subQ1=sQuery(id+"F0.wireOp",EDGE,"E3.left");var subQ2=makeQuery(id+"F0.imprint","INTERSECT",VERTEX,{"derivedFrom":[subQ1,subQ0]});Q41=makeQuery(id+"F0.imprint","IMPRINT",FACE,{"disambiguationData":[TD([[makeQuery(id+"F0.imprint","IMPRINT",EDGE,{"disambiguationData":[TD([[subQ2,-1.0]])],"derivedFrom":subQ1}),1.0]])]});}
            var Q42;
            {var subQ0=sQuery(id+"F0.wireOp",EDGE,"E11.top");Q42=makeQuery(id+"F0.imprint","IMPRINT",FACE,{"disambiguationData":[TD([[makeQuery(id+"F0.imprint","IMPRINT",EDGE,{"derivedFrom":subQ0}),1.0]])]});}
            extrude(context, id + "F4", {"entities" : qUnion([Q0, Q1, Q2, Q3, Q4, Q5, Q6, Q7, Q8, Q9, Q10, Q11, Q12, Q13, Q14, Q15, Q16, Q17, Q18, Q19, Q20, Q21, Q22, Q23, Q24, Q25, Q26, Q27, Q28, Q29, Q30, Q31, Q32, Q33, Q34, Q35, Q36, Q37, Q38, Q39, Q40, Q41, Q42]), "operationType" : NewBodyOperationType.ADD, "depth" : 4 * mm, "offsetDistance" : 25 * mm});
        }
        {
            var Q0;
            {var subQ0=sQuery(id+"F0.wireOp",EDGE,"E2.right");var subQ1=sQuery(id+"F0.wireOp",EDGE,"E2.left");Q0=makeQuery(id+"F3.boolean.opBoolean","MERGE",FACE,{"derivedFrom":[makeQuery(id+"F1.opExtrude","CAP_FACE",FACE,{"disambiguationData":[OSD([sQuery(id+"F0.wireOp",EDGE,"E0.bottom"),sQuery(id+"F0.wireOp",EDGE,"E0.top"),sQuery(id+"F0.wireOp",EDGE,"E0.left"),sQuery(id+"F0.wireOp",EDGE,"E0.right"),sQuery(id+"F0.wireOp",EDGE,"E1.0"),sQuery(id+"F0.wireOp",EDGE,"E1.1"),sQuery(id+"F0.wireOp",EDGE,"E1.2"),sQuery(id+"F0.wireOp",EDGE,"E1.3"),subQ1,subQ0,sQuery(id+"F0.wireOp",EDGE,"E3.bottom"),sQuery(id+"F0.wireOp",EDGE,"E4.bottom"),sQuery(id+"F0.wireOp",EDGE,"E6.bottom"),sQuery(id+"F0.wireOp",EDGE,"E7.bottom"),sQuery(id+"F0.wireOp",EDGE,"E8.bottom"),sQuery(id+"F0.wireOp",EDGE,"E9.left"),sQuery(id+"F0.wireOp",EDGE,"E9.right"),sQuery(id+"F0.wireOp",EDGE,"E10.left"),sQuery(id+"F0.wireOp",EDGE,"E10.right"),sQuery(id+"F0.wireOp",EDGE,"E12.left"),sQuery(id+"F0.wireOp",EDGE,"E12.right"),sQuery(id+"F0.wireOp",EDGE,"E13.left")])],"isStart":true}),makeQuery(id+"F3.opExtrude","CAP_FACE",FACE,{"disambiguationData":[OSD([sQuery(id+"F0.wireOp",EDGE,"E2.bottom"),sQuery(id+"F0.wireOp",EDGE,"E2.top"),subQ1,subQ0,sQuery(id+"F0.wireOp",EDGE,"E3.top"),sQuery(id+"F0.wireOp",EDGE,"E4.top"),sQuery(id+"F0.wireOp",EDGE,"E6.top"),sQuery(id+"F0.wireOp",EDGE,"E7.top"),sQuery(id+"F0.wireOp",EDGE,"E8.top")])],"isStart":false})]});}
            var sketch = newSketch(context, id + "F5", { "sketchPlane" : qUnion([Q0])});
            skLineSegment(sketch, "E76.bottom", {"start": v(123.41, 960) * mm, "end": v(423.41, 960) * mm});
            skLineSegment(sketch, "E76.top", {"start": v(123.41, 880) * mm, "end": v(423.41, 880) * mm});
            skLineSegment(sketch, "E76.left", {"start": v(123.41, 960) * mm, "end": v(123.41, 880) * mm});
            skLineSegment(sketch, "E76.right", {"start": v(423.41, 960) * mm, "end": v(423.41, 880) * mm});
            skSolve(sketch);
        }
        {
            var Q0;
            Q0=makeQuery(id+"F5.imprint","IMPRINT",FACE,{"disambiguationData":[TD([[makeQuery(id+"F5.imprint","IMPRINT",EDGE,{"derivedFrom":sQuery(id+"F5.wireOp",EDGE,"E76.bottom")}),-1.0]])]});
            extrude(context, id + "F6", {"entities" : qUnion([Q0]), "operationType" : NewBodyOperationType.REMOVE, "oppositeDirection" : true, "depth" : 25 * mm, "offsetDistance" : 25 * mm});
        }
        {
            var Q0;
            {var subQ0=sQuery(id+"F0.wireOp",EDGE,"E2.right");var subQ1=sQuery(id+"F0.wireOp",EDGE,"E2.left");Q0=makeQuery(id+"F3.boolean.opBoolean","MERGE",FACE,{"derivedFrom":[makeQuery(id+"F1.opExtrude","CAP_FACE",FACE,{"disambiguationData":[OSD([sQuery(id+"F0.wireOp",EDGE,"E0.bottom"),sQuery(id+"F0.wireOp",EDGE,"E0.top"),sQuery(id+"F0.wireOp",EDGE,"E0.left"),sQuery(id+"F0.wireOp",EDGE,"E0.right"),sQuery(id+"F0.wireOp",EDGE,"E1.0"),sQuery(id+"F0.wireOp",EDGE,"E1.1"),sQuery(id+"F0.wireOp",EDGE,"E1.2"),sQuery(id+"F0.wireOp",EDGE,"E1.3"),subQ1,subQ0,sQuery(id+"F0.wireOp",EDGE,"E3.bottom"),sQuery(id+"F0.wireOp",EDGE,"E4.bottom"),sQuery(id+"F0.wireOp",EDGE,"E6.bottom"),sQuery(id+"F0.wireOp",EDGE,"E7.bottom"),sQuery(id+"F0.wireOp",EDGE,"E8.bottom"),sQuery(id+"F0.wireOp",EDGE,"E9.left"),sQuery(id+"F0.wireOp",EDGE,"E9.right"),sQuery(id+"F0.wireOp",EDGE,"E10.left"),sQuery(id+"F0.wireOp",EDGE,"E10.right"),sQuery(id+"F0.wireOp",EDGE,"E12.left"),sQuery(id+"F0.wireOp",EDGE,"E12.right"),sQuery(id+"F0.wireOp",EDGE,"E13.left")])],"isStart":true}),makeQuery(id+"F3.opExtrude","CAP_FACE",FACE,{"disambiguationData":[OSD([sQuery(id+"F0.wireOp",EDGE,"E2.bottom"),sQuery(id+"F0.wireOp",EDGE,"E2.top"),subQ1,subQ0,sQuery(id+"F0.wireOp",EDGE,"E3.top"),sQuery(id+"F0.wireOp",EDGE,"E4.top"),sQuery(id+"F0.wireOp",EDGE,"E6.top"),sQuery(id+"F0.wireOp",EDGE,"E7.top"),sQuery(id+"F0.wireOp",EDGE,"E8.top")])],"isStart":false})]});}
            var sketch = newSketch(context, id + "F7", { "sketchPlane" : qUnion([Q0])});
            skCircle(sketch, "E77", {"center": v(765.68, 923.55) * mm, "radius": 31.49 * mm});
            skSolve(sketch);
        }
        {
            var Q0;
            Q0 = qSketchRegion(id + "F7", true);
            extrude(context, id + "F8", {"entities" : qUnion([Q0]), "operationType" : NewBodyOperationType.ADD, "depth" : 25 * mm, "offsetDistance" : 25 * mm});
        }
        {
            var Q0;
            Q0=makeQuery(id+"F8.opExtrude","CAP_FACE",FACE,{"disambiguationData":[OSD([sQuery(id+"F7.wireOp",EDGE,"E77")])],"isStart":false});
            var sketch = newSketch(context, id + "F9", { "sketchPlane" : qUnion([Q0])});
            skLineSegment(sketch, "E78.bottom", {"start": v(765.68, 923.55) * mm, "end": v(644.2, 923.55) * mm});
            skLineSegment(sketch, "E78.top", {"start": v(765.68, 939.78) * mm, "end": v(644.2, 939.78) * mm});
            skLineSegment(sketch, "E78.left", {"start": v(765.68, 923.55) * mm, "end": v(765.68, 939.78) * mm});
            skLineSegment(sketch, "E78.right", {"start": v(644.2, 923.55) * mm, "end": v(644.2, 939.78) * mm});
            skSolve(sketch);
        }
        {
            var Q0;
            {var subQ0=sQuery(id+"F9.wireOp",EDGE,"E78.right");Q0=makeQuery(id+"F9.imprint","IMPRINT",FACE,{"disambiguationData":[TD([[makeQuery(id+"F9.imprint","IMPRINT",EDGE,{"derivedFrom":subQ0}),-1.0]])]});}
            var Q1;
            {var subQ0=sQuery(id+"F9.wireOp",EDGE,"E78.left");Q1=makeQuery(id+"F9.imprint","IMPRINT",FACE,{"disambiguationData":[TD([[makeQuery(id+"F9.imprint","IMPRINT",EDGE,{"derivedFrom":subQ0}),1.0]])]});}
            extrude(context, id + "F10", {"entities" : qUnion([Q0, Q1]), "operationType" : NewBodyOperationType.ADD, "depth" : 25 * mm, "offsetDistance" : 25 * mm});
        }
        {
            var Q0;
            {var subQ0=sQuery(id+"F0.wireOp",EDGE,"E2.top");Q0=makeQuery(id+"F3.boolean.opBoolean","MERGE",FACE,{"derivedFrom":[makeQuery(id+"F2.opExtrude","CAP_FACE",FACE,{"disambiguationData":[OSD([sQuery(id+"F0.wireOp",EDGE,"E1.1"),sQuery(id+"F0.wireOp",EDGE,"E1.2"),sQuery(id+"F0.wireOp",EDGE,"E1.3"),subQ0])],"isStart":false}),makeQuery(id+"F3.opExtrude","CAP_FACE",FACE,{"disambiguationData":[OSD([sQuery(id+"F0.wireOp",EDGE,"E2.bottom"),subQ0,sQuery(id+"F0.wireOp",EDGE,"E2.left"),sQuery(id+"F0.wireOp",EDGE,"E2.right"),sQuery(id+"F0.wireOp",EDGE,"E3.top"),sQuery(id+"F0.wireOp",EDGE,"E4.top"),sQuery(id+"F0.wireOp",EDGE,"E6.top"),sQuery(id+"F0.wireOp",EDGE,"E7.top"),sQuery(id+"F0.wireOp",EDGE,"E8.top")])],"isStart":true})]});}
            var sketch = newSketch(context, id + "F11", { "sketchPlane" : qUnion([Q0])});
            skLineSegment(sketch, "E79.bottom", {"start": v(-423.41, 960) * mm, "end": v(-123.41, 960) * mm});
            skLineSegment(sketch, "E79.top", {"start": v(-423.41, 880) * mm, "end": v(-123.41, 880) * mm});
            skLineSegment(sketch, "E79.left", {"start": v(-423.41, 960) * mm, "end": v(-423.41, 880) * mm});
            skLineSegment(sketch, "E79.right", {"start": v(-123.41, 960) * mm, "end": v(-123.41, 880) * mm});
            skLineSegment(sketch, "E80.0", {"start": v(-435.41, 972) * mm, "end": v(-111.41, 972) * mm});
            skLineSegment(sketch, "E80.1", {"start": v(-435.41, 972) * mm, "end": v(-435.41, 868) * mm});
            skLineSegment(sketch, "E80.2", {"start": v(-435.41, 868) * mm, "end": v(-111.41, 868) * mm});
            skLineSegment(sketch, "E80.3", {"start": v(-111.41, 972) * mm, "end": v(-111.41, 868) * mm});
            skSolve(sketch);
        }
        {
            var Q0;
            Q0=makeQuery(id+"F11.imprint","IMPRINT",FACE,{"disambiguationData":[TD([[makeQuery(id+"F11.imprint","IMPRINT",EDGE,{"derivedFrom":sQuery(id+"F11.wireOp",EDGE,"E79.bottom")}),-1.0]])]});
            var Q1;
            Q1=makeQuery(id+"F11.imprint","IMPRINT",FACE,{"disambiguationData":[TD([[makeQuery(id+"F11.imprint","IMPRINT",EDGE,{"derivedFrom":sQuery(id+"F11.wireOp",EDGE,"E79.bottom")}),1.0]])]});
            extrude(context, id + "F12", {"entities" : qUnion([Q0, Q1]), "operationType" : NewBodyOperationType.ADD, "depth" : 5 * mm, "offsetDistance" : 25 * mm});
        }
    });
